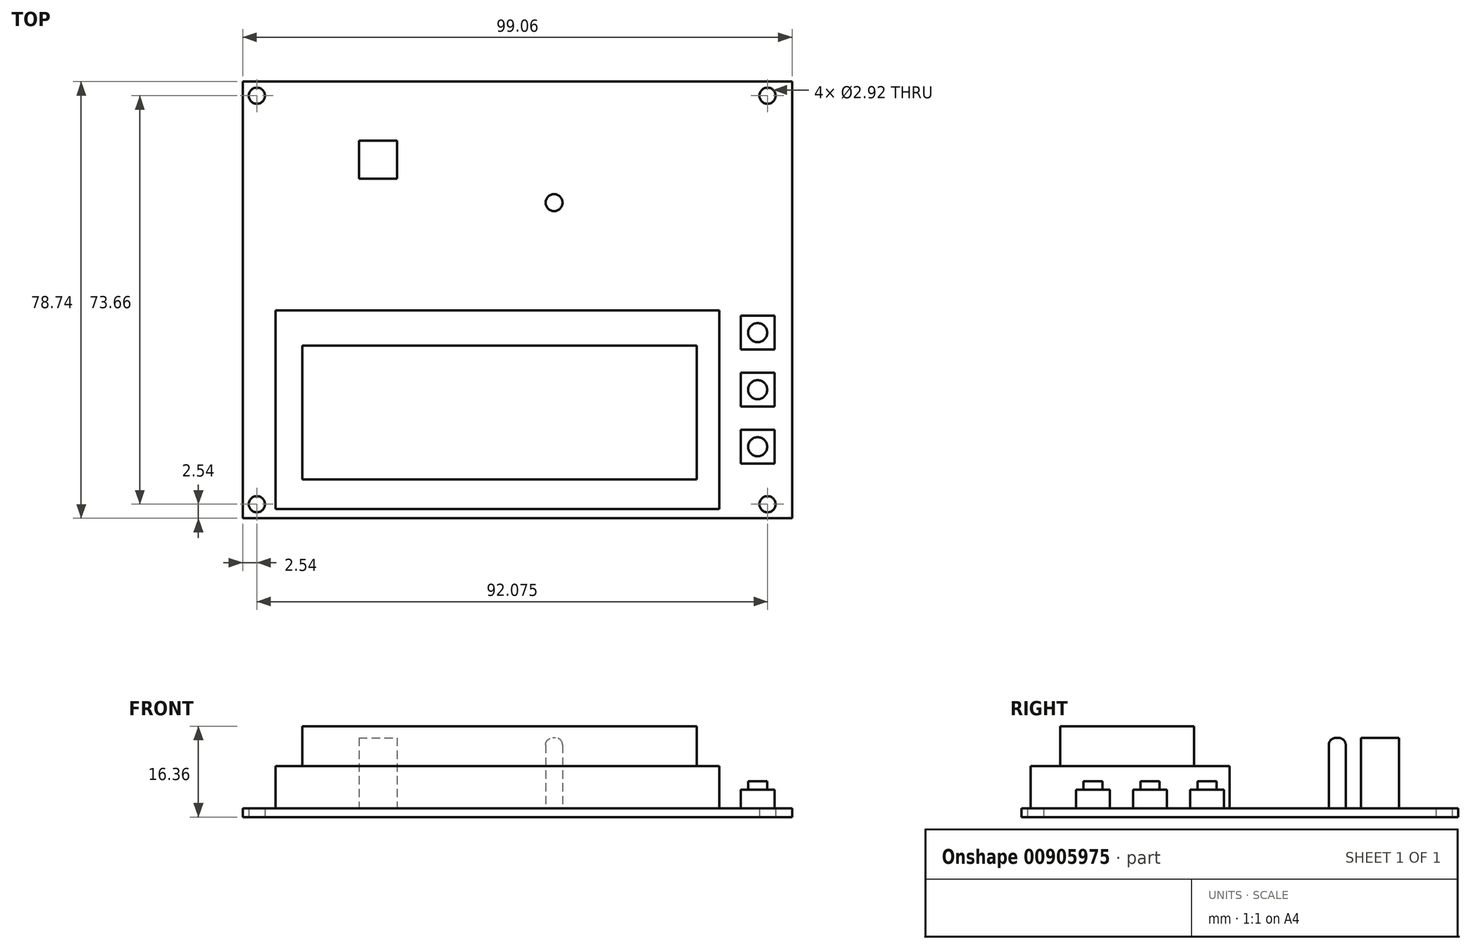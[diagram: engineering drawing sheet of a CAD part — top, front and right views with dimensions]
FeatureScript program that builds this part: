
annotation { "Feature Type Name" : "Feature", "Feature Type Description" : "" }
export const myFeature = defineFeature(function(context is Context, id is Id, definition is map)
    precondition{}
    {
        {
            var Q0;
            Q0=qCreatedBy(makeId("Top.planeOp"),FACE);
            var sketch = newSketch(context, id + "F0", { "sketchPlane" : qUnion([Q0])});
            skLineSegment(sketch, "E0.bottom", {"start": v(49.53, -39.37) * mm, "end": v(-49.53, -39.37) * mm});
            skLineSegment(sketch, "E0.top", {"start": v(49.53, 39.37) * mm, "end": v(-49.53, 39.37) * mm});
            skLineSegment(sketch, "E0.left", {"start": v(49.53, -39.37) * mm, "end": v(49.53, 39.37) * mm});
            skLineSegment(sketch, "E0.right", {"start": v(-49.53, -39.37) * mm, "end": v(-49.53, 39.37) * mm});
            skPoint(sketch, "E0.middle", {"position": v(0, 0) * mm});
            skSolve(sketch);
        }
        {
            var Q0;
            Q0 = qSketchRegion(id + "F0", true);
            extrude(context, id + "F1", {"entities" : qUnion([Q0]), "depth" : 1.57 * mm, "offsetDistance" : 25.4 * mm});
        }
        {
            var Q0;
            Q0=makeQuery(id+"F1.opExtrude","CAP_FACE",FACE,{"disambiguationData":[OSD([sQuery(id+"F0.wireOp",EDGE,"E0.bottom"),sQuery(id+"F0.wireOp",EDGE,"E0.top"),sQuery(id+"F0.wireOp",EDGE,"E0.left"),sQuery(id+"F0.wireOp",EDGE,"E0.right")])],"isStart":false});
            var sketch = newSketch(context, id + "F2", { "sketchPlane" : qUnion([Q0])});
            skLineSegment(sketch, "E1.bottom", {"start": v(-43.64, -37.72) * mm, "end": v(36.37, -37.72) * mm});
            skLineSegment(sketch, "E1.top", {"start": v(-43.64, -1.85) * mm, "end": v(36.37, -1.85) * mm});
            skLineSegment(sketch, "E1.left", {"start": v(-43.64, -37.72) * mm, "end": v(-43.64, -1.85) * mm});
            skLineSegment(sketch, "E1.right", {"start": v(36.37, -37.72) * mm, "end": v(36.37, -1.85) * mm});
            skSolve(sketch);
        }
        {
            var Q0;
            Q0 = qSketchRegion(id + "F2", true);
            extrude(context, id + "F3", {"entities" : qUnion([Q0]), "operationType" : NewBodyOperationType.ADD, "depth" : 7.62 * mm, "offsetDistance" : 25.4 * mm});
        }
        {
            var Q0;
            Q0=makeQuery(id+"F3.opExtrude","CAP_FACE",FACE,{"disambiguationData":[OSD([sQuery(id+"F2.wireOp",EDGE,"E1.bottom"),sQuery(id+"F2.wireOp",EDGE,"E1.top"),sQuery(id+"F2.wireOp",EDGE,"E1.left"),sQuery(id+"F2.wireOp",EDGE,"E1.right")])],"isStart":false});
            var sketch = newSketch(context, id + "F4", { "sketchPlane" : qUnion([Q0])});
            skLineSegment(sketch, "E2.bottom", {"start": v(-38.81, -8.26) * mm, "end": v(32.3, -8.25) * mm});
            skLineSegment(sketch, "E2.top", {"start": v(-38.81, -32.39) * mm, "end": v(32.3, -32.39) * mm});
            skLineSegment(sketch, "E2.left", {"start": v(-38.81, -8.26) * mm, "end": v(-38.81, -32.39) * mm});
            skLineSegment(sketch, "E2.right", {"start": v(32.3, -8.25) * mm, "end": v(32.3, -32.39) * mm});
            skSolve(sketch);
        }
        {
            var Q0;
            Q0 = qSketchRegion(id + "F4", true);
            extrude(context, id + "F5", {"entities" : qUnion([Q0]), "operationType" : NewBodyOperationType.ADD, "depth" : 7.16 * mm, "offsetDistance" : 25.4 * mm});
        }
        {
            var Q0;
            Q0=makeQuery(id+"F1.opExtrude","CAP_FACE",FACE,{"disambiguationData":[OSD([sQuery(id+"F0.wireOp",EDGE,"E0.bottom"),sQuery(id+"F0.wireOp",EDGE,"E0.top"),sQuery(id+"F0.wireOp",EDGE,"E0.left"),sQuery(id+"F0.wireOp",EDGE,"E0.right")])],"isStart":false});
            var sketch = newSketch(context, id + "F6", { "sketchPlane" : qUnion([Q0])});
            skLineSegment(sketch, "E3.bottom", {"start": v(40.26, -23.42) * mm, "end": v(46.35, -23.42) * mm});
            skLineSegment(sketch, "E3.top", {"start": v(40.26, -29.51) * mm, "end": v(46.36, -29.51) * mm});
            skLineSegment(sketch, "E3.left", {"start": v(40.26, -23.42) * mm, "end": v(40.26, -29.51) * mm});
            skLineSegment(sketch, "E3.right", {"start": v(46.36, -23.42) * mm, "end": v(46.36, -29.51) * mm});
            skLineSegment(sketch, "E4.bottom", {"start": v(40.26, -19.23) * mm, "end": v(46.35, -19.23) * mm});
            skLineSegment(sketch, "E4.top", {"start": v(40.26, -13.13) * mm, "end": v(46.35, -13.13) * mm});
            skLineSegment(sketch, "E4.left", {"start": v(40.26, -19.23) * mm, "end": v(40.26, -13.13) * mm});
            skLineSegment(sketch, "E4.right", {"start": v(46.35, -19.23) * mm, "end": v(46.35, -13.13) * mm});
            skLineSegment(sketch, "E5.bottom", {"start": v(40.26, -8.94) * mm, "end": v(46.35, -8.94) * mm});
            skLineSegment(sketch, "E5.top", {"start": v(40.26, -2.84) * mm, "end": v(46.35, -2.84) * mm});
            skLineSegment(sketch, "E5.left", {"start": v(40.26, -8.94) * mm, "end": v(40.26, -2.84) * mm});
            skLineSegment(sketch, "E5.right", {"start": v(46.35, -8.94) * mm, "end": v(46.35, -2.84) * mm});
            skSolve(sketch);
        }
        {
            var Q0;
            Q0 = qSketchRegion(id + "F6", true);
            extrude(context, id + "F7", {"entities" : qUnion([Q0]), "operationType" : NewBodyOperationType.ADD, "depth" : 3.38 * mm, "offsetDistance" : 25.4 * mm});
        }
        {
            var Q0;
            Q0=makeQuery(id+"F7.opExtrude","CAP_FACE",FACE,{"disambiguationData":[OSD([sQuery(id+"F6.wireOp",EDGE,"E5.bottom"),sQuery(id+"F6.wireOp",EDGE,"E5.top"),sQuery(id+"F6.wireOp",EDGE,"E5.left"),sQuery(id+"F6.wireOp",EDGE,"E5.right")])],"isStart":false});
            var sketch = newSketch(context, id + "F8", { "sketchPlane" : qUnion([Q0])});
            skLineSegment(sketch, "E6", {"start": v(40.26, -2.84) * mm, "end": v(46.35, -8.94) * mm, "construction": true});
            skCircle(sketch, "E7", {"center": v(43.3, -5.9) * mm, "radius": 1.71 * mm});
            skLineSegment(sketch, "E8.0", {"start": v(40.26, -13.13) * mm, "end": v(46.35, -13.13) * mm, "construction": true});
            skLineSegment(sketch, "E9.0", {"start": v(40.26, -19.23) * mm, "end": v(46.35, -19.23) * mm, "construction": true});
            skLineSegment(sketch, "E10.0", {"start": v(40.26, -23.42) * mm, "end": v(46.35, -23.42) * mm, "construction": true});
            skLineSegment(sketch, "E11.0", {"start": v(40.26, -29.51) * mm, "end": v(46.36, -29.51) * mm, "construction": true});
            skLineSegment(sketch, "E12", {"start": v(40.26, -13.13) * mm, "end": v(46.35, -19.23) * mm, "construction": true});
            skLineSegment(sketch, "E13", {"start": v(40.26, -23.42) * mm, "end": v(46.36, -29.51) * mm, "construction": true});
            skCircle(sketch, "E14", {"center": v(43.3, -16.18) * mm, "radius": 1.71 * mm});
            skCircle(sketch, "E15", {"center": v(43.3, -26.47) * mm, "radius": 1.71 * mm});
            skSolve(sketch);
        }
        {
            var Q0;
            Q0=makeQuery(id+"F8.imprint","IMPRINT",FACE,{"disambiguationData":[TD([[makeQuery(id+"F8.imprint","IMPRINT",EDGE,{"derivedFrom":sQuery(id+"F8.wireOp",EDGE,"E7")}),1.0]])]});
            var Q1;
            Q1=makeQuery(id+"F8.imprint","IMPRINT",FACE,{"disambiguationData":[TD([[makeQuery(id+"F8.imprint","IMPRINT",EDGE,{"derivedFrom":sQuery(id+"F8.wireOp",EDGE,"E14")}),1.0]])]});
            var Q2;
            Q2=makeQuery(id+"F8.imprint","IMPRINT",FACE,{"disambiguationData":[TD([[makeQuery(id+"F8.imprint","IMPRINT",EDGE,{"derivedFrom":sQuery(id+"F8.wireOp",EDGE,"E15")}),1.0]])]});
            extrude(context, id + "F9", {"entities" : qUnion([Q0, Q1, Q2]), "operationType" : NewBodyOperationType.ADD, "depth" : 1.52 * mm, "offsetDistance" : 25.4 * mm});
        }
        {
            var Q0;
            Q0=makeQuery(id+"F1.opExtrude","CAP_FACE",FACE,{"disambiguationData":[OSD([sQuery(id+"F0.wireOp",EDGE,"E0.bottom"),sQuery(id+"F0.wireOp",EDGE,"E0.top"),sQuery(id+"F0.wireOp",EDGE,"E0.left"),sQuery(id+"F0.wireOp",EDGE,"E0.right")])],"isStart":false});
            var sketch = newSketch(context, id + "F10", { "sketchPlane" : qUnion([Q0])});
            skCircle(sketch, "E16", {"center": v(6.6, 17.55) * mm, "radius": 1.52 * mm});
            skSolve(sketch);
        }
        {
            var Q0;
            Q0 = qSketchRegion(id + "F10", true);
            extrude(context, id + "F11", {"entities" : qUnion([Q0]), "operationType" : NewBodyOperationType.ADD, "depth" : 12.7 * mm, "offsetDistance" : 25.4 * mm});
        }
        {
            var Q0;
            Q0=makeQuery(id+"F11.opExtrude","CAP_EDGE",EDGE,{"disambiguationData":[OSD([sQuery(id+"F10.wireOp",EDGE,"E16")])],"isStart":false});
            fillet(context, id + "F12", {"entities" : qUnion([Q0]), "radius" : 1.27 * mm, "tangentPropagation" : true, "allowEdgeOverflow" : false});
        }
        {
            var Q0;
            Q0=makeQuery(id+"F1.opExtrude","CAP_FACE",FACE,{"disambiguationData":[OSD([sQuery(id+"F0.wireOp",EDGE,"E0.bottom"),sQuery(id+"F0.wireOp",EDGE,"E0.top"),sQuery(id+"F0.wireOp",EDGE,"E0.left"),sQuery(id+"F0.wireOp",EDGE,"E0.right")])],"isStart":false});
            var sketch = newSketch(context, id + "F13", { "sketchPlane" : qUnion([Q0])});
            skLineSegment(sketch, "E17.bottom", {"start": v(-28.58, 28.7) * mm, "end": v(-21.72, 28.7) * mm});
            skLineSegment(sketch, "E17.top", {"start": v(-28.58, 21.84) * mm, "end": v(-21.72, 21.84) * mm});
            skLineSegment(sketch, "E17.left", {"start": v(-28.58, 28.7) * mm, "end": v(-28.58, 21.84) * mm});
            skLineSegment(sketch, "E17.right", {"start": v(-21.72, 28.7) * mm, "end": v(-21.72, 21.84) * mm});
            skSolve(sketch);
        }
        {
            var Q0;
            Q0=makeQuery(id+"F13.imprint","IMPRINT",FACE,{"disambiguationData":[TD([[makeQuery(id+"F13.imprint","IMPRINT",EDGE,{"derivedFrom":sQuery(id+"F13.wireOp",EDGE,"E17.bottom")}),-1.0]])]});
            extrude(context, id + "F14", {"entities" : qUnion([Q0]), "operationType" : NewBodyOperationType.ADD, "depth" : 12.7 * mm, "offsetDistance" : 25.4 * mm});
        }
        {
            var Q0;
            Q0=makeQuery(id+"F1.opExtrude","CAP_FACE",FACE,{"disambiguationData":[OSD([sQuery(id+"F0.wireOp",EDGE,"E0.bottom"),sQuery(id+"F0.wireOp",EDGE,"E0.top"),sQuery(id+"F0.wireOp",EDGE,"E0.left"),sQuery(id+"F0.wireOp",EDGE,"E0.right")])],"isStart":true});
            var sketch = newSketch(context, id + "F15", { "sketchPlane" : qUnion([Q0])});
            skLineSegment(sketch, "E18.bottom", {"start": v(-47, 36.83) * mm, "end": v(45.08, 36.83) * mm, "construction": true});
            skLineSegment(sketch, "E18.top", {"start": v(-47, -36.83) * mm, "end": v(45.08, -36.83) * mm, "construction": true});
            skLineSegment(sketch, "E18.left", {"start": v(-47, 36.83) * mm, "end": v(-47, -36.83) * mm, "construction": true});
            skLineSegment(sketch, "E18.right", {"start": v(45.08, 36.83) * mm, "end": v(45.08, -36.83) * mm, "construction": true});
            skCircle(sketch, "E19", {"center": v(-47, 36.83) * mm, "radius": 1.46 * mm});
            skCircle(sketch, "E20", {"center": v(45.08, 36.83) * mm, "radius": 1.46 * mm});
            skCircle(sketch, "E21", {"center": v(45.08, -36.83) * mm, "radius": 1.46 * mm});
            skCircle(sketch, "E22", {"center": v(-47, -36.83) * mm, "radius": 1.46 * mm});
            skSolve(sketch);
        }
        {
            var Q0;
            Q0 = qSketchRegion(id + "F15", true);
            extrude(context, id + "F16", {"entities" : qUnion([Q0]), "operationType" : NewBodyOperationType.REMOVE, "endBound" : BoundingType.UP_TO_NEXT, "oppositeDirection" : true, "depth" : 25.4 * mm, "offsetDistance" : 25.4 * mm});
        }
    });
